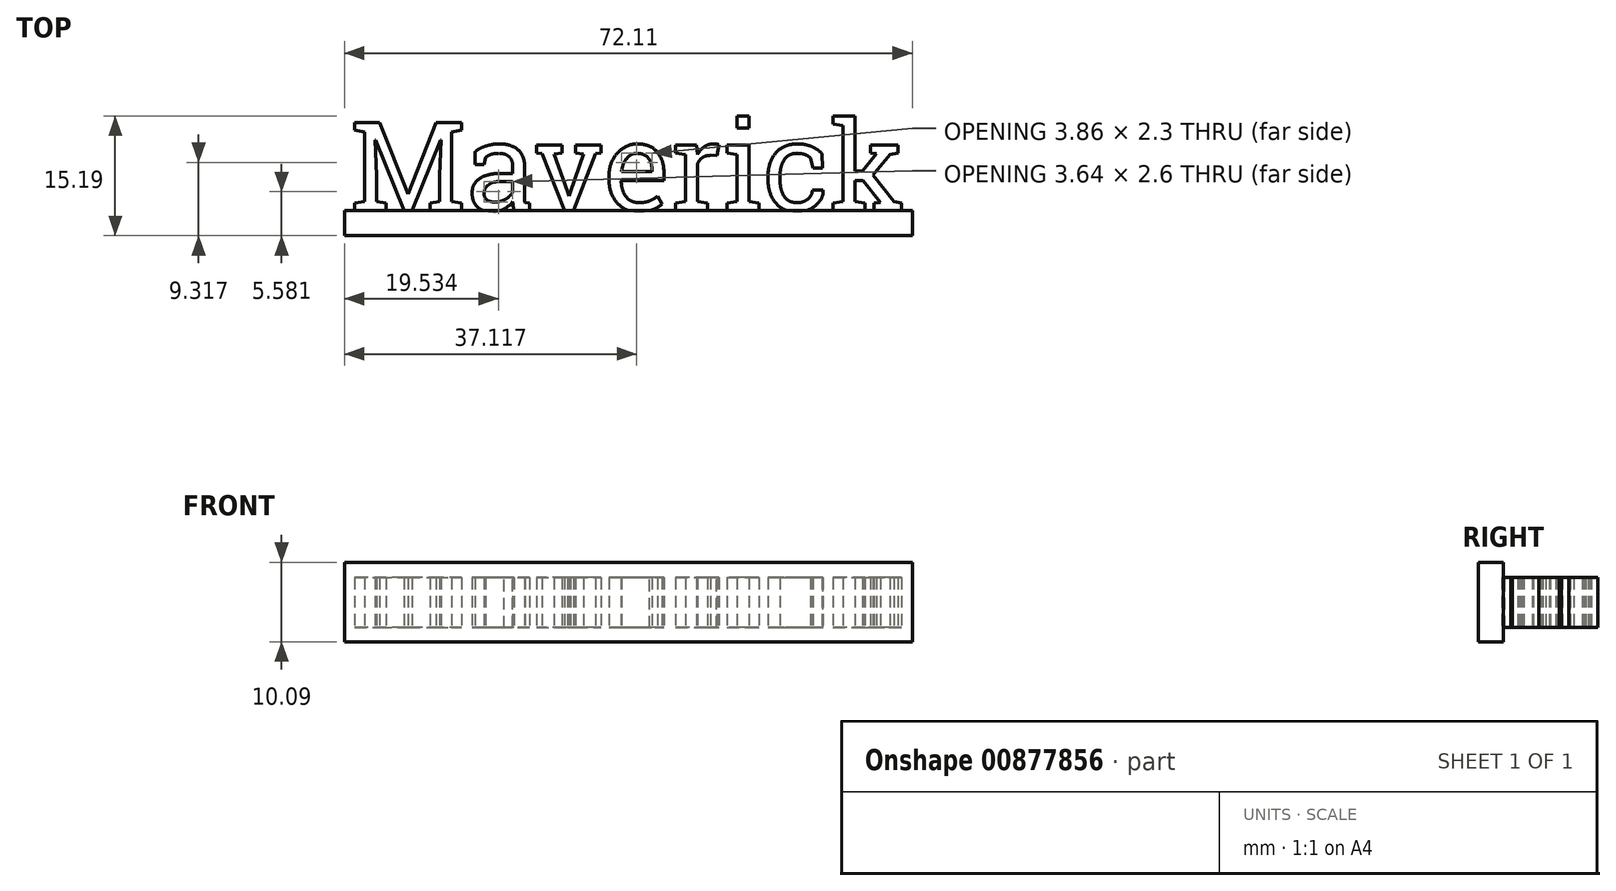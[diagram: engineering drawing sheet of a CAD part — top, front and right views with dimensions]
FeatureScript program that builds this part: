
annotation { "Feature Type Name" : "Feature", "Feature Type Description" : "" }
export const myFeature = defineFeature(function(context is Context, id is Id, definition is map)
    precondition{}
    {
        {
            var Q0;
            Q0=qCreatedBy(makeId("Top.planeOp"),FACE);
            var sketch = newSketch(context, id + "F0", { "sketchPlane" : qUnion([Q0])});
            skText(sketch, "E0", { "text": "Maverick", "fontName": "RobotoSlab-Regular.ttf"});
            const initialGuessF0  = {"E0": [-0.03413, 0, 1, 0, 0.01136]};
            skSetInitialGuess(sketch, initialGuessF0);
            skSolve(sketch);
        }
        {
            var Q0;
            Q0 = qSketchRegion(id + "F0", true);
            extrude(context, id + "F1", {"entities" : qUnion([Q0]), "depth" : 6.35 * mm, "offsetDistance" : 25.4 * mm});
        }
        {
            var Q0;
            Q0=qCreatedBy(makeId("Front.planeOp"),FACE);
            var sketch = newSketch(context, id + "F2", { "sketchPlane" : qUnion([Q0])});
            skLineSegment(sketch, "E1.bottom", {"start": v(-34.85, 8.29) * mm, "end": v(37.26, 8.29) * mm});
            skLineSegment(sketch, "E1.top", {"start": v(-34.85, -1.8) * mm, "end": v(37.26, -1.8) * mm});
            skLineSegment(sketch, "E1.left", {"start": v(-34.85, 8.29) * mm, "end": v(-34.85, -1.8) * mm});
            skLineSegment(sketch, "E1.right", {"start": v(37.26, 8.29) * mm, "end": v(37.26, -1.8) * mm});
            skSolve(sketch);
        }
        {
            var Q0;
            Q0=makeQuery(id+"F2.imprint","IMPRINT",FACE,{"disambiguationData":[TD([[makeQuery(id+"F2.imprint","IMPRINT",EDGE,{"derivedFrom":sQuery(id+"F2.wireOp",EDGE,"E1.bottom")}),-1.0]])]});
            extrude(context, id + "F3", {"entities" : qUnion([Q0]), "depth" : 3.17 * mm, "offsetDistance" : 25.4 * mm});
        }
    });
